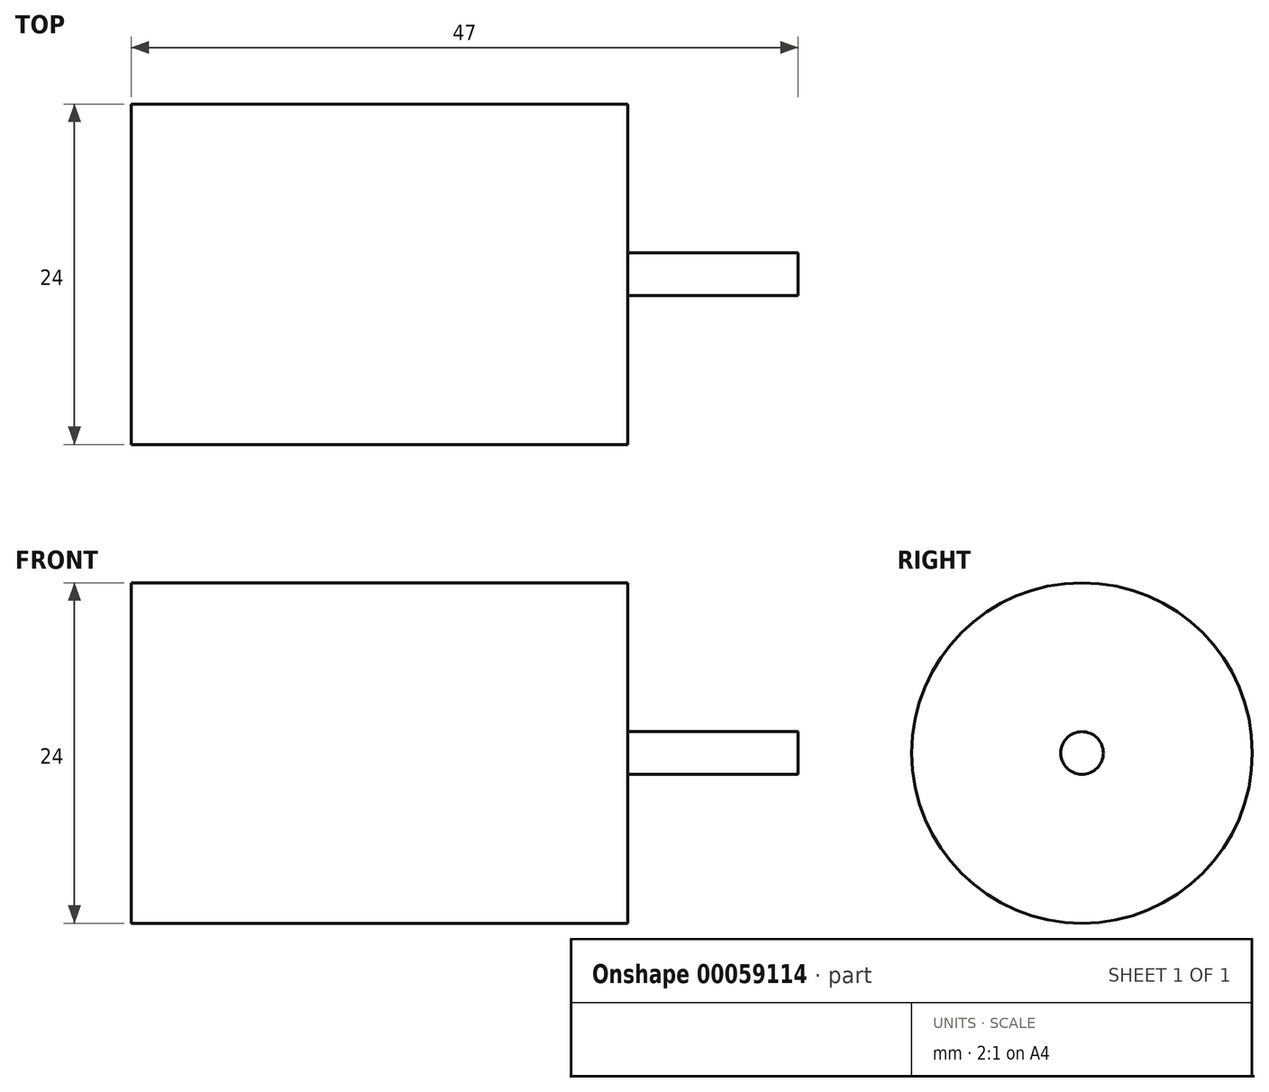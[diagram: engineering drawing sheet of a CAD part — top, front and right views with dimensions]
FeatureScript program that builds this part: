
annotation { "Feature Type Name" : "Feature", "Feature Type Description" : "" }
export const myFeature = defineFeature(function(context is Context, id is Id, definition is map)
    precondition{}
    {
        {
            var Q0;
            Q0=qCreatedBy(makeId("Right.planeOp"),FACE);
            var sketch = newSketch(context, id + "F0", { "sketchPlane" : qUnion([Q0])});
            skCircle(sketch, "E0", {"center": v(0, 0) * mm, "radius": 12 * mm});
            skSolve(sketch);
        }
        {
            var Q0;
            Q0 = qSketchRegion(id + "F0", true);
            extrude(context, id + "F1", {"entities" : qUnion([Q0]), "depth" : 35 * mm});
        }
        {
            var Q0;
            Q0=makeQuery(id+"F1.opExtrude","CAP_FACE",FACE,{"disambiguationData":[OSD([sQuery(id+"F0.wireOp",EDGE,"E0")])],"isStart":false});
            var sketch = newSketch(context, id + "F2", { "sketchPlane" : qUnion([Q0])});
            skCircle(sketch, "E1", {"center": v(0, 0) * mm, "radius": 1.5 * mm});
            skSolve(sketch);
        }
        {
            var Q0;
            Q0 = qSketchRegion(id + "F2", true);
            extrude(context, id + "F3", {"entities" : qUnion([Q0]), "operationType" : NewBodyOperationType.ADD, "depth" : 12 * mm});
        }
    });
